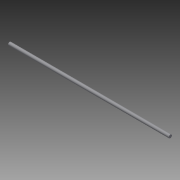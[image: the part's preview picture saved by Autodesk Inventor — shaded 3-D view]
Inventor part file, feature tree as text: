
AUTODESK INVENTOR PART (.ipt)
format: ipt  version: 2015 (Build 190159000, 159)  size: 64,512 bytes
history: native  units: in
note: dims shown in document units (in); Inventor stores cm internally (conversion verified against a paired STEP export)
features: extrude x1, sketch x1
ambient origin geometry x8: Origin, YZ Plane, XZ Plane, XY Plane, X Axis, Y Axis, Z Axis, Center Point
bodies: Solid1 (feature_tree)
feature tree (2):
  extrude  "Extrusion1"  Depth=12.3125in TaperAngle=0.0deg
  sketch  "Sketch1"  dims[d0=0.25in d1=12.3125in d2=0.0in]
